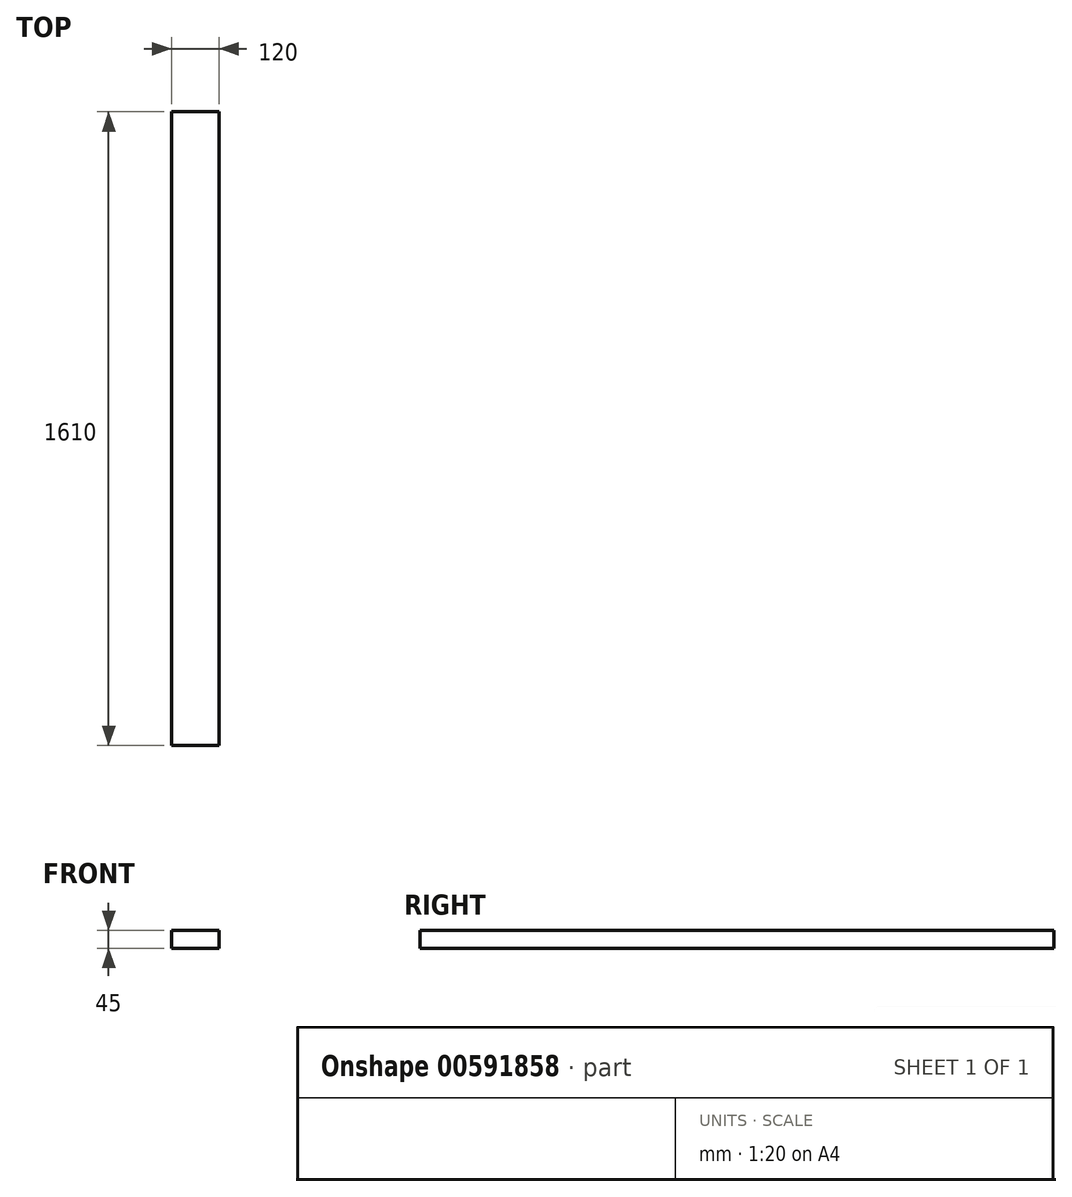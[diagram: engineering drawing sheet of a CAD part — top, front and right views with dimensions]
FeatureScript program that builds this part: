
annotation { "Feature Type Name" : "Feature", "Feature Type Description" : "" }
export const myFeature = defineFeature(function(context is Context, id is Id, definition is map)
    precondition{}
    {
        {
            var Q0;
            Q0=qCreatedBy(makeId("Top.planeOp"),FACE);
            var sketch = newSketch(context, id + "F0", { "sketchPlane" : qUnion([Q0])});
            skLineSegment(sketch, "E0.bottom", {"start": v(0, 0) * mm, "end": v(-120, 0) * mm});
            skLineSegment(sketch, "E0.top", {"start": v(0, 1610) * mm, "end": v(-120, 1610) * mm});
            skLineSegment(sketch, "E0.left", {"start": v(0, 0) * mm, "end": v(0, 1610) * mm});
            skLineSegment(sketch, "E0.right", {"start": v(-120, 0) * mm, "end": v(-120, 1610) * mm});
            skSolve(sketch);
        }
        {
            var Q0;
            Q0=makeQuery(id+"F0.imprint","IMPRINT",FACE,{"disambiguationData":[TD([[makeQuery(id+"F0.imprint","IMPRINT",EDGE,{"derivedFrom":sQuery(id+"F0.wireOp",EDGE,"E0.bottom")}),-1.0]])]});
            extrude(context, id + "F1", {"entities" : qUnion([Q0]), "depth" : 45 * mm, "offsetDistance" : 25 * mm});
        }
    });
